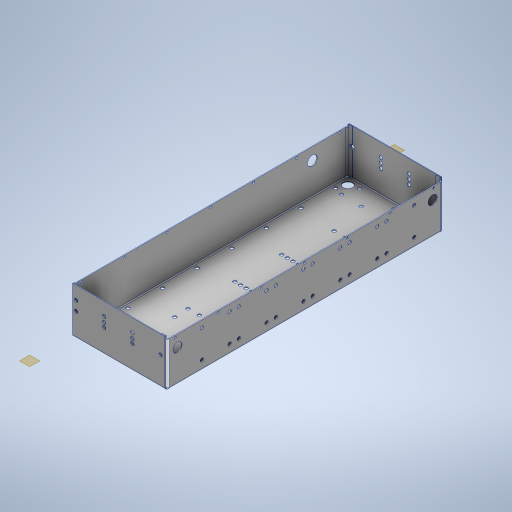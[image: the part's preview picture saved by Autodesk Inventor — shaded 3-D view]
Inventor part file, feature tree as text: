
AUTODESK INVENTOR PART (.ipt)
format: ipt  version: 2023 (Build 270158000, 158)  size: 800,768 bytes
history: native  units: in
note: dims shown in document units (in); Inventor stores cm internally (conversion verified against a paired STEP export)
features: sketch x26, hole x20, sheet_metal_op x12, pattern_linear x12, other x8, plane x4
ambient origin geometry x8: Origin, YZ Plane, XZ Plane, XY Plane, X Axis, Y Axis, Z Axis, Center Point
bodies: Solid1 (feature_tree)
feature tree (82):
  sheet_metal_op  "Face1"
  sheet_metal_op  "Flange1"
  sheet_metal_op  "Flange2"
  sheet_metal_op  "Unfold1"
  hole  "Hole1"  [1 undecoded]
  pattern_linear  "Rectangular Pattern1"  Count1=30  [1 undecoded]
  pattern_linear  "Rectangular Pattern2"  Count1=10  [1 undecoded]
  hole  "Hole2"  [1 undecoded]
  pattern_linear  "Rectangular Pattern3"  Count1=10 Spacing1=90.0deg
  hole  "Hole3"  [1 undecoded]
  hole  "Hole6"  [1 undecoded]
  pattern_linear  "Rectangular Pattern6"  Count1=10 Spacing1=90.0deg
  plane  "Work Plane4"
  hole  "Hole7"  [1 undecoded]
  plane  "Work Plane3"
  hole  "Hole8"  [1 undecoded]
  plane  "Work Plane2"
  hole  "Hole9"  [1 undecoded]
  plane  "Work Plane1"
  hole  "Hole10"  [1 undecoded]
  hole  "Hole11"  [1 undecoded]
  hole  "Hole12"  [1 undecoded]
  hole  "Hole13"  [1 undecoded]
  pattern_linear  "Rectangular Pattern11"  Count1=6  [1 undecoded]
  pattern_linear  "Rectangular Pattern12"  Count1=6  [1 undecoded]
  pattern_linear  "Rectangular Pattern13"  Count1=6  [1 undecoded]
  pattern_linear  "Rectangular Pattern14"  Count1=2  [1 undecoded]
  sheet_metal_op  "Refold6"
  sheet_metal_op  "Flange8"
  hole  "Hole14"  [1 undecoded]
  hole  "Hole15"  [1 undecoded]
  hole  "Hole16"  [1 undecoded]
  hole  "Hole17"  [1 undecoded]
  hole  "Hole18"  [1 undecoded]
  hole  "Hole19"  [1 undecoded]
  pattern_linear  "Rectangular Pattern15"  Count1=3  [1 undecoded]
  hole  "Hole20"  [1 undecoded]
  pattern_linear  "Rectangular Pattern16"  Count1=3  [1 undecoded]
  hole  "Hole22"  [1 undecoded]
  pattern_linear  "Rectangular Pattern18"  Count1=3  [1 undecoded]
  hole  "Hole21"  [1 undecoded]
  pattern_linear  "Rectangular Pattern17"  Spacing1=0.374in  [1 undecoded]
  sketch  "Sketch1"  dims[d0=23.622in d1=7.874in d2=11.811in d3=3.937in]
  other  "Plate1"
  sketch  "Sketch2"  dims[d4=0.0625in d5=0.0625in]
  other  "Plate2"
  sheet_metal_op  "Bend1"
  sheet_metal_op  "Corner1"
  sketch  "Sketch3"  dims[d6=0.0312in]
  other  "Plate3"
  sheet_metal_op  "Bend2"
  sheet_metal_op  "Corner2"
  sketch  "Sketch5"  dims[d7=0.125in]
  sketch  "Sketch6"  dims[d8=0.0625in d9=3.937in d10=90.0deg d11=0.0787in]
  sketch  "Sketch7"  dims[d12=0.25in d13=0.0625in]
  sketch  "Sketch10"  dims[d14=0.0625in d15=0.0625in]
  sketch  "Sketch11"  dims[d16=0.0312in]
  sketch  "Sketch13"  dims[d17=0.125in]
  sketch  "Sketch15"  dims[d18=0.0625in d19=3.937in d20=90.0deg d21=0.0787in]
  sketch  "Sketch16"  dims[d22=0.25in d23=0.0625in]
  sketch  "Sketch17"  dims[d24=0.0625in]
  sketch  "Sketch21"  dims[d35=0.2969in d36=0.2953in d37=0.1476in d38=0.0984in d39=90.0deg d40=0.0625in d41=0.8108in]
  sketch  "Sketch25"  dims[d42=0.7874in d44=0.9646in d46=1.1811in d48=3.9921in]
  sketch  "Sketch26"  dims[d49=0.2969in d50=0.2953in d51=0.1476in d52=0.0984in d53=90.0deg d54=0.3937in d55=0.8108in d56=0.9646in]
  other  "Plate9"
  sheet_metal_op  "Bend8"
  sheet_metal_op  "Corner8"
  sketch  "Sketch27"  dims[d57=0.9646in d58=0.4823in]
  sketch  "Sketch28"  dims[d59=1.1811in d61=3.9921in]
  sketch  "Sketch29"  dims[d62=0.7874in d63=0.2953in d64=0.1476in d65=0.0984in d66=90.0deg d67=0.3937in d68=0.8108in d69=0.5906in]
  sketch  "Sketch30"  dims[d70=0.5906in]
  sketch  "Sketch31"  dims[d95=0.2969in d96=0.2953in d97=0.1476in d98=0.0984in d99=90.0deg d100=0.0625in d101=0.8108in d102=2.3622in d103=2.3622in d104=2.3622in d105=0.7874in]
  sketch  "Sketch32"  dims[d106=2.3622in d107=2.3622in d109=3.1496in]
  sketch  "Sketch33"  dims[d110=0.2969in d111=0.2953in d112=0.1476in d113=0.0984in d114=90.0deg d115=0.0625in d116=0.8108in]
  sketch  "Sketch34"  dims[d122=0.2969in d123=0.2953in d124=0.1476in d125=0.0984in d126=90.0deg d127=0.3937in d128=0.8108in d129=0.8071in]
  sketch  "Sketch35"  dims[d130=0.4035in]
  sketch  "Sketch36"  dims[d134=0.2969in d135=0.2953in d136=0.1476in d137=0.0984in d138=90.0deg d139=0.3937in d140=0.8108in]
  sketch  "Sketch37"  dims[d144=0.2969in d145=0.2953in d146=0.1476in d147=0.0984in d148=90.0deg d149=0.3937in d150=0.8108in d151=0.8071in d158=0.2969in d159=0.2953in d160=0.1476in d161=0.0984in d162=90.0deg d163=0.3937in d164=0.8108in d165=1.9252in d166=2.6949in d167=1.1811in d168=0.9626in d169=0.7874in d170=0.2953in d171=0.1476in d172=0.0984in d173=90.0deg d174=0.3937in d175=0.8108in d176=0.7874in d177=0.2953in d178=0.1476in d179=0.0984in d180=90.0deg d181=0.3937in d182=0.8108in d183=1.1811in d184=0.7874in d185=1.1811in d186=0.7874in d188=0.374in d189=2.433in d190=0.3346in d191=2.433in d192=1.1811in d194=2.4016in d195=1.1811in d197=2.4016in d198=1.1811in d200=2.4016in d201=1.1811in d203=2.4016in d205=7.0866in d206=0.5316in d231=0.0984in d250=0.0in d263=0.0in d265=0.0in d271=0.0625in d272=0.0in d273=0.0625in d274=0.0in d275=0.0625in d276=0.0312in d277=0.125in d278=0.0625in d279=0.5in d280=90.0deg d281=0.0984in d282=0.25in d283=0.0625in d284=0.0625in d285=7.874in d286=2.4016in d287=0.4331in d288=0.2953in d289=0.1476in d290=0.0984in d291=90.0deg d292=0.0625in d293=0.0in d294=0.4331in d295=0.2953in d296=0.1476in d297=0.0984in d298=90.0deg d299=0.3937in d300=0.0in d301=0.8386in d302=0.2953in d303=0.1476in d304=0.0984in d305=90.0deg d306=0.0625in d307=0.8108in d308=0.2969in d309=0.2953in d310=0.1476in d311=0.0984in d312=90.0deg d313=0.3937in d314=0.8108in d316=2.2441in d319=0.2969in d320=0.2953in d321=0.1476in d322=0.0984in d323=90.0deg d324=0.3937in d325=0.8108in d326=1.0236in d327=1.5748in d328=2.9528in d329=2.5591in d330=1.0236in d331=2.7559in d332=0.5906in d333=0.0in d334=0.2969in d335=0.2953in d336=0.1476in d337=0.0984in d338=90.0deg d339=0.0625in d340=0.8108in d341=0.5in d342=1.5in d343=3.1496in d345=2.9528in d346=0.7874in d348=7.2065in d349=0.2969in d350=0.2953in d351=0.1476in d352=0.0984in d353=90.0deg d354=0.0625in d355=0.8108in d356=0.5in d357=1.5in d358=1.1811in d360=2.9528in d361=0.7874in d363=22.622in d364=0.194in d365=0.2953in d366=0.1476in d367=0.0984in d368=90.0deg d369=0.0625in d370=0.8108in d371=0.5in d372=2.7559in d374=3.6755in d377=0.0625in d378=0.0in d379=0.194in d380=0.2953in d381=0.1476in d382=0.0984in d383=90.0deg d384=0.0625in d385=0.8108in d386=0.5in d387=0.162in d388=2.7559in d390=3.6755in d392=0.0625in d393=0.0in d394=0.162in d395=0.2073in d397=0.2073in]
  other  "Cut4"
  other  "Cut5"
  other  "Cut6"
  other  "Cut7"
note: 30 required parameter values undecoded (feature->parameter linkage not recoverable at this tier; creation-order binding heuristic only, values carry confidence <= 0.55)
